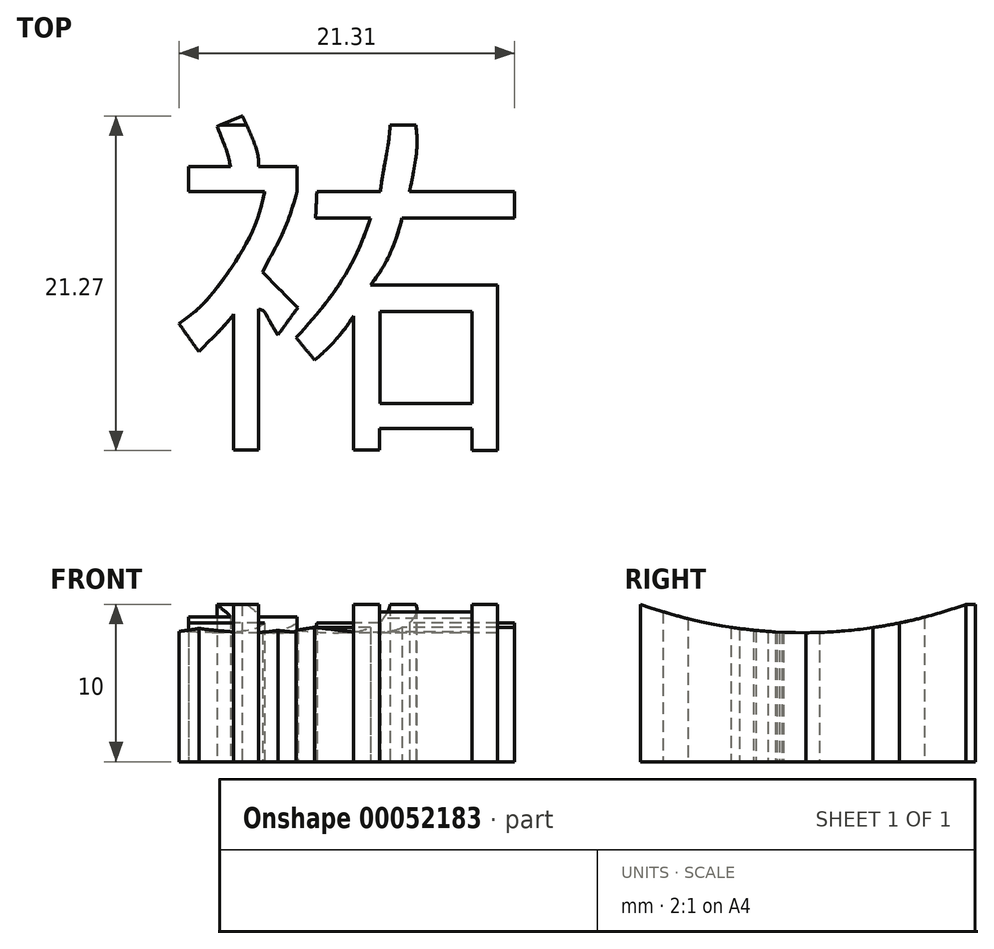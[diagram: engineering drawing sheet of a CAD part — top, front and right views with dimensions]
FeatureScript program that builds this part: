
annotation { "Feature Type Name" : "Feature", "Feature Type Description" : "" }
export const myFeature = defineFeature(function(context is Context, id is Id, definition is map)
    precondition{}
    {
        {
            var Q0;
            Q0=qCreatedBy(makeId("Top.planeOp"),FACE);
            var sketch = newSketch(context, id + "F0", { "sketchPlane" : qUnion([Q0])});
            skLineSegment(sketch, "E0.bottom", {"start": v(15.2, -44.35) * mm, "end": v(45.2, -44.35) * mm, "construction": true});
            skLineSegment(sketch, "E0.top", {"start": v(15.2, -74.35) * mm, "end": v(45.2, -74.35) * mm, "construction": true});
            skLineSegment(sketch, "E0.left", {"start": v(15.2, -44.35) * mm, "end": v(15.2, -74.35) * mm, "construction": true});
            skLineSegment(sketch, "E0.right", {"start": v(45.2, -44.35) * mm, "end": v(45.2, -74.35) * mm, "construction": true});
            skLineSegment(sketch, "E1", {"start": v(21.38, -48.84) * mm, "end": v(22.97, -48.17) * mm});
            skLineSegment(sketch, "E2", {"start": v(19.58, -51.4) * mm, "end": v(19.58, -53) * mm});
            skLineSegment(sketch, "E3", {"start": v(19.58, -51.4) * mm, "end": v(22.22, -51.4) * mm});
            skLineSegment(sketch, "E4", {"start": v(24.02, -51.4) * mm, "end": v(26.46, -51.4) * mm});
            skLineSegment(sketch, "E5", {"start": v(26.46, -51.4) * mm, "end": v(26.46, -53) * mm});
            skLineSegment(sketch, "E6", {"start": v(19.58, -53) * mm, "end": v(24.4, -53) * mm});
            skLineSegment(sketch, "E7", {"start": v(27.71, -53) * mm, "end": v(31.74, -53) * mm});
            skLineSegment(sketch, "E8", {"start": v(32.37, -48.76) * mm, "end": v(34, -48.76) * mm});
            skLineSegment(sketch, "E9", {"start": v(33.59, -53) * mm, "end": v(40.26, -53) * mm});
            skLineSegment(sketch, "E10", {"start": v(40.26, -53) * mm, "end": v(40.26, -54.67) * mm});
            skLineSegment(sketch, "E11", {"start": v(40.26, -54.67) * mm, "end": v(33.13, -54.67) * mm});
            skLineSegment(sketch, "E12", {"start": v(31.11, -54.67) * mm, "end": v(27.63, -54.67) * mm});
            skLineSegment(sketch, "E13", {"start": v(27.63, -54.67) * mm, "end": v(27.71, -53) * mm});
            skLineSegment(sketch, "E14", {"start": v(31.11, -58.92) * mm, "end": v(39.19, -58.92) * mm});
            skLineSegment(sketch, "E15", {"start": v(39.19, -58.92) * mm, "end": v(39.19, -69.44) * mm});
            skLineSegment(sketch, "E16", {"start": v(39.19, -69.44) * mm, "end": v(37.55, -69.44) * mm});
            skLineSegment(sketch, "E17", {"start": v(37.55, -69.44) * mm, "end": v(37.55, -68.01) * mm});
            skLineSegment(sketch, "E18", {"start": v(37.55, -68.01) * mm, "end": v(31.68, -68.01) * mm});
            skLineSegment(sketch, "E19", {"start": v(31.68, -68.01) * mm, "end": v(31.68, -69.39) * mm});
            skLineSegment(sketch, "E20", {"start": v(31.68, -69.39) * mm, "end": v(30.04, -69.39) * mm});
            skLineSegment(sketch, "E21", {"start": v(30.04, -69.39) * mm, "end": v(30.04, -60.88) * mm});
            skLineSegment(sketch, "E22", {"start": v(22.43, -60.77) * mm, "end": v(22.43, -69.39) * mm});
            skLineSegment(sketch, "E23", {"start": v(22.43, -69.39) * mm, "end": v(24.02, -69.39) * mm});
            skLineSegment(sketch, "E24", {"start": v(24.02, -69.39) * mm, "end": v(24.02, -60.45) * mm});
            skLineSegment(sketch, "E25", {"start": v(18.95, -61.35) * mm, "end": v(20.21, -63.15) * mm});
            skLineSegment(sketch, "E26", {"start": v(25.23, -62.1) * mm, "end": v(26.5, -60.35) * mm});
            skLineSegment(sketch, "E27", {"start": v(26.4, -62.25) * mm, "end": v(27.56, -63.68) * mm});
            skLineSegment(sketch, "E28.bottom", {"start": v(31.74, -66.43) * mm, "end": v(37.55, -66.43) * mm});
            skLineSegment(sketch, "E28.top", {"start": v(31.74, -60.61) * mm, "end": v(37.55, -60.61) * mm});
            skLineSegment(sketch, "E28.left", {"start": v(31.74, -66.43) * mm, "end": v(31.74, -60.61) * mm});
            skLineSegment(sketch, "E28.right", {"start": v(37.55, -66.43) * mm, "end": v(37.55, -60.61) * mm});
            skFitSpline(sketch, "E29", {"points": [v(22.97, -48.17) * mm, v(23.54, -49.4) * mm, v(23.97, -50.68) * mm, v(24.02, -51.4) * mm], "startDerivative": vector(1.58, -3.28) * mm, "endDerivative": vector(0.02, -2.5) * mm});
            skFitSpline(sketch, "E30", {"points": [v(21.38, -48.84) * mm, v(21.8, -49.9) * mm, v(22.06, -50.62) * mm, v(22.22, -51.4) * mm], "startDerivative": vector(1.15, -2.98) * mm, "endDerivative": vector(0.44, -2.56) * mm});
            skFitSpline(sketch, "E31", {"points": [v(24.4, -53) * mm, v(23.93, -54.75) * mm, v(22.96, -56.76) * mm, v(21.2, -59.3) * mm, v(19.88, -60.68) * mm, v(18.95, -61.35) * mm], "startDerivative": vector(-2.08, -9.18) * mm, "endDerivative": vector(-6.04, -3.97) * mm});
            skFitSpline(sketch, "E32", {"points": [v(26.46, -53) * mm, v(25.63, -55.44) * mm, v(24.6, -57.45) * mm, v(24.27, -58.08) * mm], "startDerivative": vector(-1.74, -6) * mm, "endDerivative": vector(-1.25, -2.54) * mm});
            skFitSpline(sketch, "E33", {"points": [v(24.27, -58.08) * mm, v(25.31, -59.18) * mm, v(26.5, -60.35) * mm], "startDerivative": vector(2.1, -2.25) * mm, "endDerivative": vector(2.37, -2.3) * mm});
            skFitSpline(sketch, "E34", {"points": [v(26.4, -62.25) * mm, v(28.08, -60.3) * mm, v(29.82, -57.77) * mm, v(30.62, -56.03) * mm, v(31.11, -54.67) * mm], "startDerivative": vector(6.16, 6.8) * mm, "endDerivative": vector(2.34, 6.63) * mm});
            skFitSpline(sketch, "E35", {"points": [v(25.23, -62.1) * mm, v(24.92, -61.56) * mm, v(24.59, -60.97) * mm, v(24.33, -60.57) * mm, v(24.02, -60.45) * mm], "startDerivative": vector(-1.15, 1.9) * mm, "endDerivative": vector(-1.66, 0.34) * mm});
            skFitSpline(sketch, "E36", {"points": [v(22.43, -60.77) * mm, v(21.74, -61.6) * mm, v(20.8, -62.55) * mm, v(20.21, -63.15) * mm], "startDerivative": vector(-1.92, -2.44) * mm, "endDerivative": vector(-1.82, -1.93) * mm});
            skFitSpline(sketch, "E37", {"points": [v(33.13, -54.67) * mm, v(32.66, -56.2) * mm, v(31.87, -57.84) * mm, v(31.11, -58.92) * mm], "startDerivative": vector(-1.22, -4.46) * mm, "endDerivative": vector(-2.5, -3.28) * mm});
            skFitSpline(sketch, "E38", {"points": [v(30.04, -60.88) * mm, v(29.3, -61.95) * mm, v(28.06, -63.26) * mm, v(27.56, -63.68) * mm], "startDerivative": vector(-1.87, -2.94) * mm, "endDerivative": vector(-1.78, -1.4) * mm});
            skFitSpline(sketch, "E39", {"points": [v(33.59, -53) * mm, v(33.9, -51.52) * mm, v(34.07, -49.98) * mm, v(34, -48.76) * mm], "startDerivative": vector(0.94, 4.23) * mm, "endDerivative": vector(-0.36, 3.82) * mm});
            skFitSpline(sketch, "E40", {"points": [v(32.37, -48.76) * mm, v(32.21, -50.18) * mm, v(31.91, -51.8) * mm, v(31.74, -53) * mm], "startDerivative": vector(-0.37, -4.13) * mm, "endDerivative": vector(-0.47, -3.72) * mm});
            skSolve(sketch);
        }
        {
            var Q0;
            Q0=makeQuery(id+"F0.imprint","IMPRINT",FACE,{"disambiguationData":[TD([[makeQuery(id+"F0.imprint","IMPRINT",EDGE,{"derivedFrom":sQuery(id+"F0.wireOp",EDGE,"E1")}),-1.0]])]});
            var Q1;
            Q1=makeQuery(id+"F0.imprint","IMPRINT",FACE,{"disambiguationData":[TD([[makeQuery(id+"F0.imprint","IMPRINT",EDGE,{"derivedFrom":sQuery(id+"F0.wireOp",EDGE,"E7")}),-1.0]])]});
            extrude(context, id + "F1", {"entities" : qUnion([Q0, Q1]), "depth" : 10 * mm});
        }
        {
            var Q0;
            Q0=qCreatedBy(makeId("Right.planeOp"),FACE);
            var sketch = newSketch(context, id + "F2", { "sketchPlane" : qUnion([Q0])});
            skArc(sketch, "E41", {"start": v(-69.44, 10) * mm, "mid": v(-59.1, 8.2) * mm, "end": v(-48.76, 10) * mm});
            skLineSegment(sketch, "E42.0", {"start": v(-58.92, 10) * mm, "end": v(-69.44, 10) * mm});
            skFitSpline(sketch, "E43.0", {"points": [v(-54.67, 10) * mm, v(-55.17, 10) * mm, v(-56.2, 10) * mm, v(-57.86, 10) * mm, v(-58.59, 10) * mm, v(-58.92, 10) * mm]});
            skPoint(sketch, "E44.0", {"position": v(-53, 10) * mm});
            skFitSpline(sketch, "E45.0", {"points": [v(-53, 10) * mm, v(-52.51, 10) * mm, v(-51.54, 10) * mm, v(-49.99, 10) * mm, v(-49.15, 10) * mm, v(-48.76, 10) * mm]});
            skLineSegment(sketch, "E46.0", {"start": v(-53, 10) * mm, "end": v(-54.67, 10) * mm});
            skCircle(sketch, "E47", {"center": v(-59.1, 38.64) * mm, "radius": 30.45 * mm});
            skSolve(sketch);
        }
        {
            var Q0;
            {var subQ1=sQuery(id+"F2.wireOp",EDGE,"E42.0");Q0=makeQuery(id+"F2.imprint","IMPRINT",FACE,{"disambiguationData":[TD([[makeQuery(id+"F2.imprint","IMPRINT",EDGE,{"derivedFrom":subQ1}),1.0]])]});}
            extrude(context, id + "F3", {"entities" : qUnion([Q0]), "operationType" : NewBodyOperationType.REMOVE, "depth" : 200 * mm});
        }
    });
